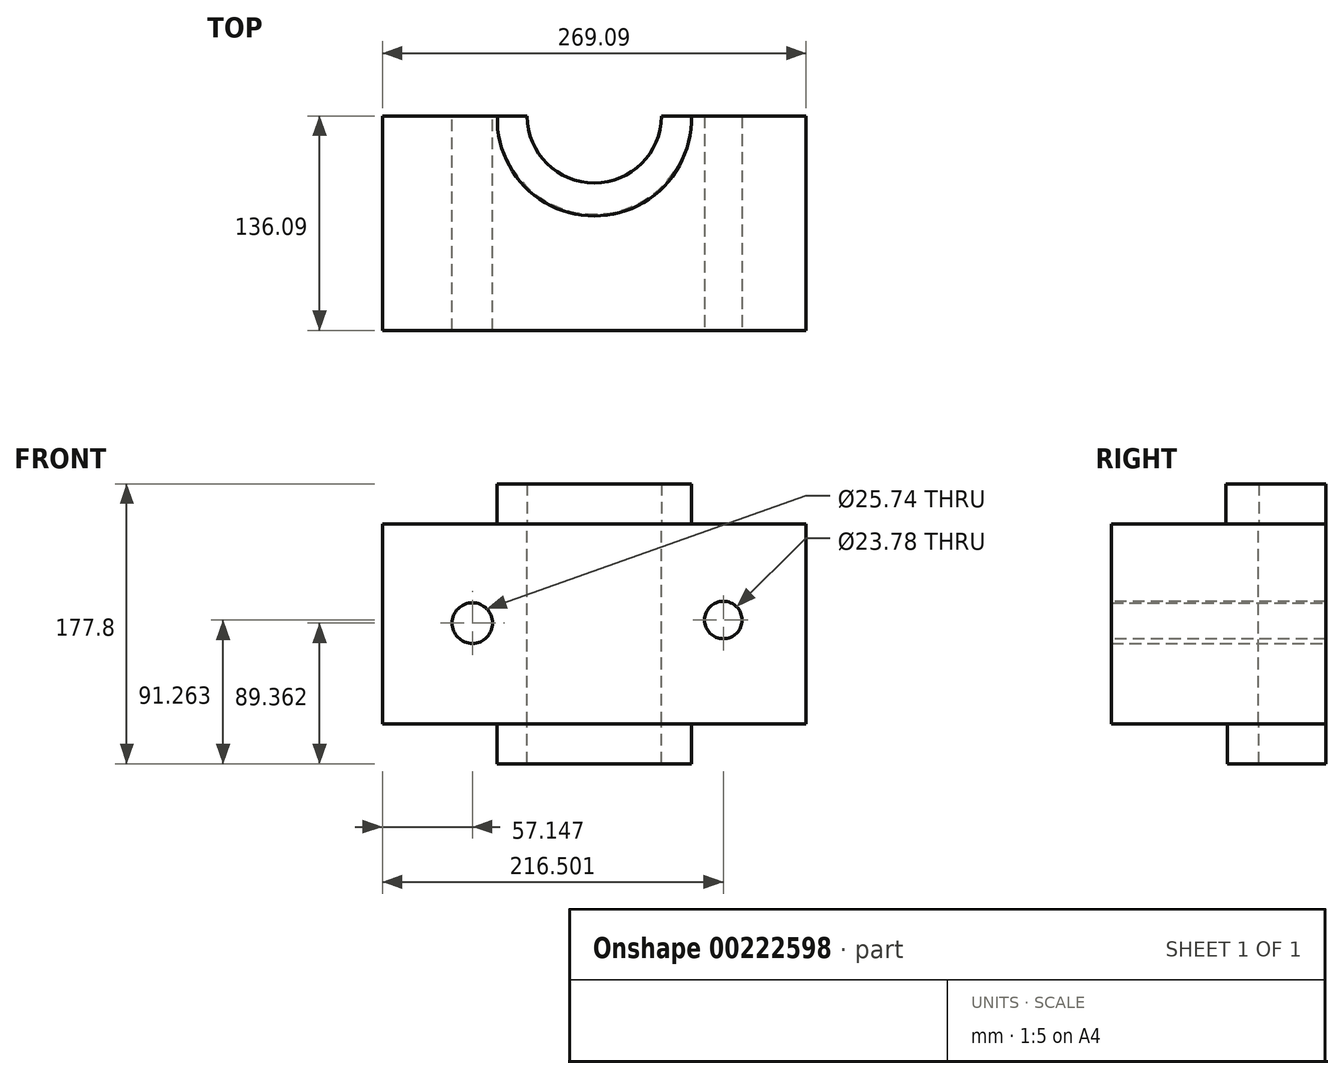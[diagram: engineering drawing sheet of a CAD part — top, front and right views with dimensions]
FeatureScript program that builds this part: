
annotation { "Feature Type Name" : "Feature", "Feature Type Description" : "" }
export const myFeature = defineFeature(function(context is Context, id is Id, definition is map)
    precondition{}
    {
        {
            var Q0;
            Q0=qCreatedBy(makeId("Top.planeOp"),FACE);
            var sketch = newSketch(context, id + "F0", { "sketchPlane" : qUnion([Q0])});
            skLineSegment(sketch, "E0.bottom", {"start": v(-155.53, 50.15) * mm, "end": v(113.56, 50.15) * mm});
            skLineSegment(sketch, "E0.top", {"start": v(-155.53, -85.94) * mm, "end": v(113.56, -85.94) * mm});
            skLineSegment(sketch, "E0.left", {"start": v(-155.53, 50.15) * mm, "end": v(-155.53, -85.94) * mm});
            skLineSegment(sketch, "E0.right", {"start": v(113.56, 50.15) * mm, "end": v(113.56, -85.94) * mm});
            skSolve(sketch);
        }
        {
            var Q0;
            Q0 = qSketchRegion(id + "F0", true);
            extrude(context, id + "F1", {"entities" : qUnion([Q0]), "depth" : 127 * mm});
        }
        {
            var Q0;
            Q0=makeQuery(id+"F1.opExtrude","CAP_FACE",FACE,{"disambiguationData":[OSD([sQuery(id+"F0.wireOp",EDGE,"E0.bottom"),sQuery(id+"F0.wireOp",EDGE,"E0.top"),sQuery(id+"F0.wireOp",EDGE,"E0.left"),sQuery(id+"F0.wireOp",EDGE,"E0.right")])],"isStart":false});
            var sketch = newSketch(context, id + "F2", { "sketchPlane" : qUnion([Q0])});
            skCircle(sketch, "E1", {"center": v(-20.99, 50.15) * mm, "radius": 42.62 * mm});
            skSolve(sketch);
        }
        {
            var Q0;
            Q0 = qSketchRegion(id + "F2", true);
            extrude(context, id + "F3", {"entities" : qUnion([Q0]), "operationType" : NewBodyOperationType.REMOVE, "endBound" : BoundingType.THROUGH_ALL, "oppositeDirection" : true, "depth" : 25.4 * mm});
        }
        {
            var Q0;
            Q0=makeQuery(id+"F1.opExtrude","CAP_FACE",FACE,{"disambiguationData":[OSD([sQuery(id+"F0.wireOp",EDGE,"E0.bottom"),sQuery(id+"F0.wireOp",EDGE,"E0.top"),sQuery(id+"F0.wireOp",EDGE,"E0.left"),sQuery(id+"F0.wireOp",EDGE,"E0.right")])],"isStart":true});
            var sketch = newSketch(context, id + "F4", { "sketchPlane" : qUnion([Q0])});
            skLineSegment(sketch, "E2", {"start": v(40.62, -50.15) * mm, "end": v(21.64, -50.15) * mm});
            skLineSegment(sketch, "E3", {"start": v(-63.61, -50.15) * mm, "end": v(-82.6, -50.15) * mm});
            skArc(sketch, "E4", {"start": v(40.62, -50.15) * mm, "mid": v(-20.99, 12.18) * mm, "end": v(-82.6, -50.15) * mm});
            skArc(sketch, "E5", {"start": v(21.64, -50.15) * mm, "mid": v(-20.99, -7.68) * mm, "end": v(-63.61, -50.15) * mm});
            skSolve(sketch);
        }
        {
            var Q0;
            Q0 = qSketchRegion(id + "F4", true);
            extrude(context, id + "F5", {"entities" : qUnion([Q0]), "operationType" : NewBodyOperationType.ADD, "depth" : 25.4 * mm});
        }
        {
            var Q0;
            Q0=makeQuery(id+"F1.opExtrude","CAP_FACE",FACE,{"disambiguationData":[OSD([sQuery(id+"F0.wireOp",EDGE,"E0.bottom"),sQuery(id+"F0.wireOp",EDGE,"E0.top"),sQuery(id+"F0.wireOp",EDGE,"E0.left"),sQuery(id+"F0.wireOp",EDGE,"E0.right")])],"isStart":false});
            var sketch = newSketch(context, id + "F6", { "sketchPlane" : qUnion([Q0])});
            skLineSegment(sketch, "E6", {"start": v(-63.61, 50.15) * mm, "end": v(-82.6, 50.15) * mm});
            skLineSegment(sketch, "E7", {"start": v(21.64, 50.15) * mm, "end": v(40.62, 50.15) * mm});
            skArc(sketch, "E8", {"start": v(-82.6, 50.15) * mm, "mid": v(-20.99, -13.3) * mm, "end": v(40.62, 50.15) * mm});
            skArc(sketch, "E9", {"start": v(-63.61, 50.15) * mm, "mid": v(-20.99, 7.63) * mm, "end": v(21.64, 50.15) * mm});
            skSolve(sketch);
        }
        {
            var Q0;
            Q0 = qSketchRegion(id + "F6", true);
            extrude(context, id + "F7", {"entities" : qUnion([Q0]), "operationType" : NewBodyOperationType.ADD, "depth" : 25.4 * mm});
        }
        {
            var Q0;
            {var subQ1=sQuery(id+"F0.wireOp",EDGE,"E0.left");var subQ3=sQuery(id+"F0.wireOp",EDGE,"E0.bottom");Q0=makeQuery(id+"F7.boolean.opBoolean","MERGE",FACE,{"derivedFrom":[makeQuery(id+"F5.boolean.opBoolean","MERGE",FACE,{"derivedFrom":[makeQuery(id+"F3.boolean.opBoolean","SPLIT",FACE,{"disambiguationData":[TD([makeQuery(id+"F1.opExtrude","SWEPT_FACE",FACE,{"disambiguationData":[OSD([subQ1])]})])],"derivedFrom":makeQuery(id+"F1.opExtrude","SWEPT_FACE",FACE,{"disambiguationData":[OSD([subQ3])]})}),makeQuery(id+"F5.opExtrude","SWEPT_FACE",FACE,{"disambiguationData":[OSD([sQuery(id+"F4.wireOp",EDGE,"E3")])]})]}),makeQuery(id+"F7.opExtrude","SWEPT_FACE",FACE,{"disambiguationData":[OSD([sQuery(id+"F6.wireOp",EDGE,"E6")])]})]});}
            var sketch = newSketch(context, id + "F8", { "sketchPlane" : qUnion([Q0])});
            skCircle(sketch, "E10", {"center": v(98.38, 63.96) * mm, "radius": 12.87 * mm});
            skSolve(sketch);
        }
        {
            var Q0;
            Q0 = qSketchRegion(id + "F8", true);
            extrude(context, id + "F9", {"entities" : qUnion([Q0]), "operationType" : NewBodyOperationType.REMOVE, "endBound" : BoundingType.THROUGH_ALL, "oppositeDirection" : true, "depth" : 25.4 * mm});
        }
        {
            var Q0;
            Q0=makeQuery(id+"F1.opExtrude","SWEPT_FACE",FACE,{"disambiguationData":[OSD([sQuery(id+"F0.wireOp",EDGE,"E0.top")])]});
            var sketch = newSketch(context, id + "F10", { "sketchPlane" : qUnion([Q0])});
            skCircle(sketch, "E11", {"center": v(60.97, 65.86) * mm, "radius": 11.89 * mm});
            skSolve(sketch);
        }
        {
            var Q0;
            Q0 = qSketchRegion(id + "F10", true);
            extrude(context, id + "F11", {"entities" : qUnion([Q0]), "operationType" : NewBodyOperationType.REMOVE, "endBound" : BoundingType.THROUGH_ALL, "oppositeDirection" : true, "depth" : 25.4 * mm});
        }
    });
